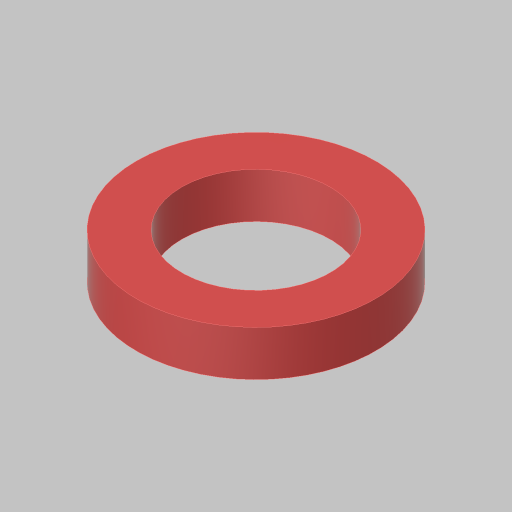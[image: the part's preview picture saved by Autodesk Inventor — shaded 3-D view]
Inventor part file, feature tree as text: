
AUTODESK INVENTOR PART (.ipt)
format: ipt  version: 2023.5 (Build 275446000, 446)  size: 96,768 bytes
history: native  units: in
note: dims shown in document units (in); Inventor stores cm internally (conversion verified against a paired STEP export)
features: extrude x1, sketch x1
ambient origin geometry x8: Origin, YZ Plane, XZ Plane, XY Plane, X Axis, Y Axis, Z Axis, Center Point
bodies: Solid1 (feature_tree)
feature tree (2):
  extrude  "Extrusion1"  Depth=0.125in
  sketch  "Sketch1"  dims[d0=0.41in d1=0.125in d2=0.125in d3=0.0in]
